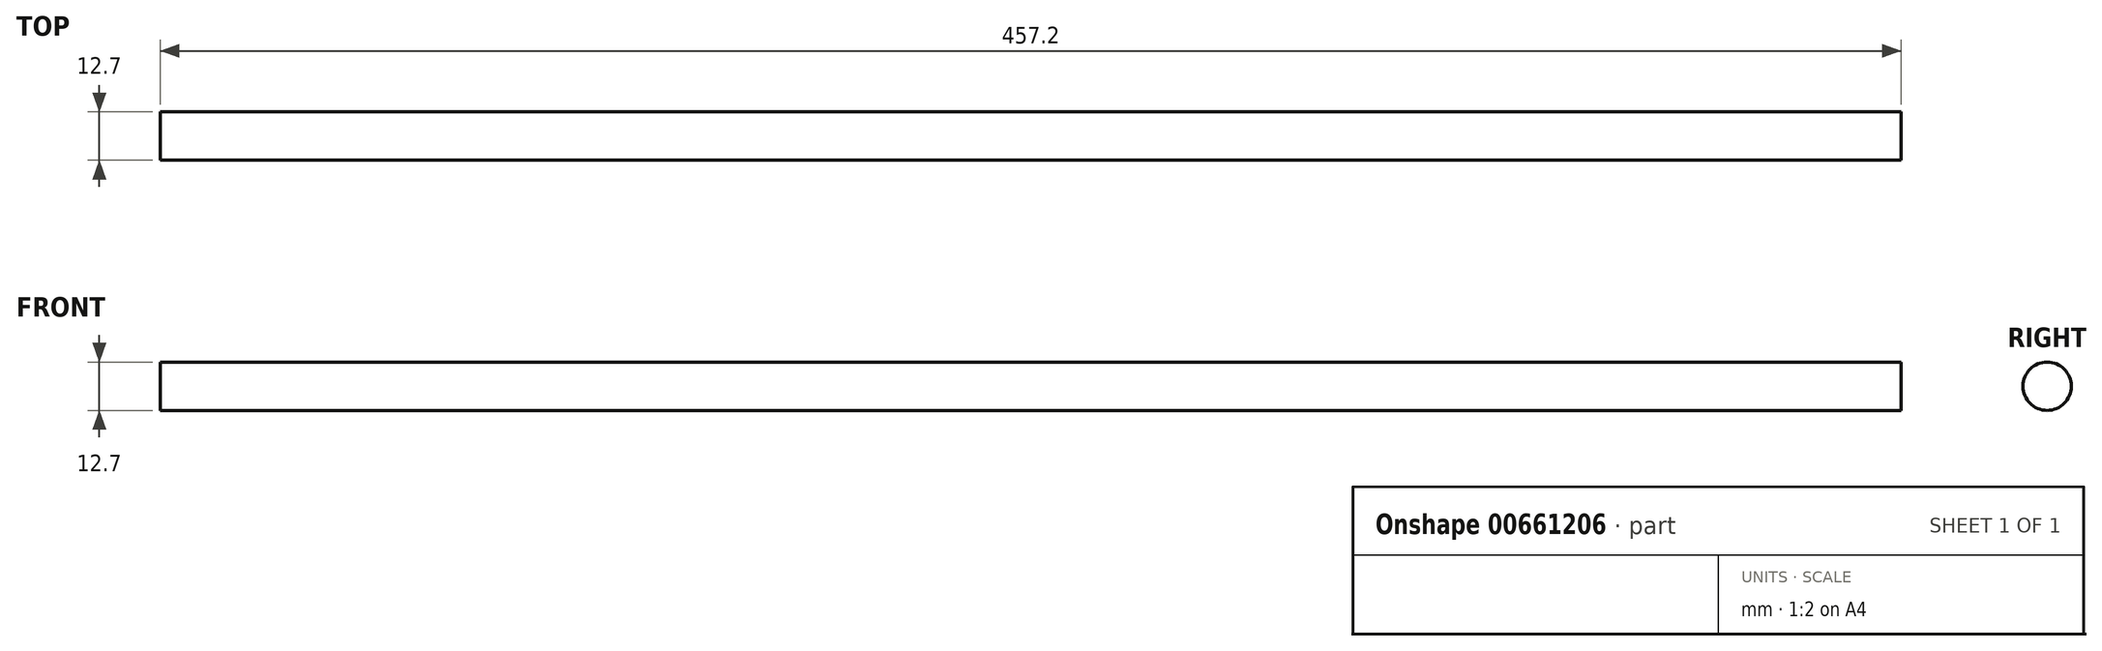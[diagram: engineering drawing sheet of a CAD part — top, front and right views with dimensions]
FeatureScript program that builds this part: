
annotation { "Feature Type Name" : "Feature", "Feature Type Description" : "" }
export const myFeature = defineFeature(function(context is Context, id is Id, definition is map)
    precondition{}
    {
        {
            var Q0;
            Q0=qCreatedBy(makeId("Right.planeOp"),FACE);
            var sketch = newSketch(context, id + "F0", { "sketchPlane" : qUnion([Q0])});
            skCircle(sketch, "E0", {"center": v(0, 0) * mm, "radius": 6.35 * mm});
            skSolve(sketch);
        }
        {
            var Q0;
            Q0 = qSketchRegion(id + "F0", true);
            extrude(context, id + "F1", {"entities" : qUnion([Q0]), "depth" : 457.2 * mm, "offsetDistance" : 25.4 * mm});
        }
    });
